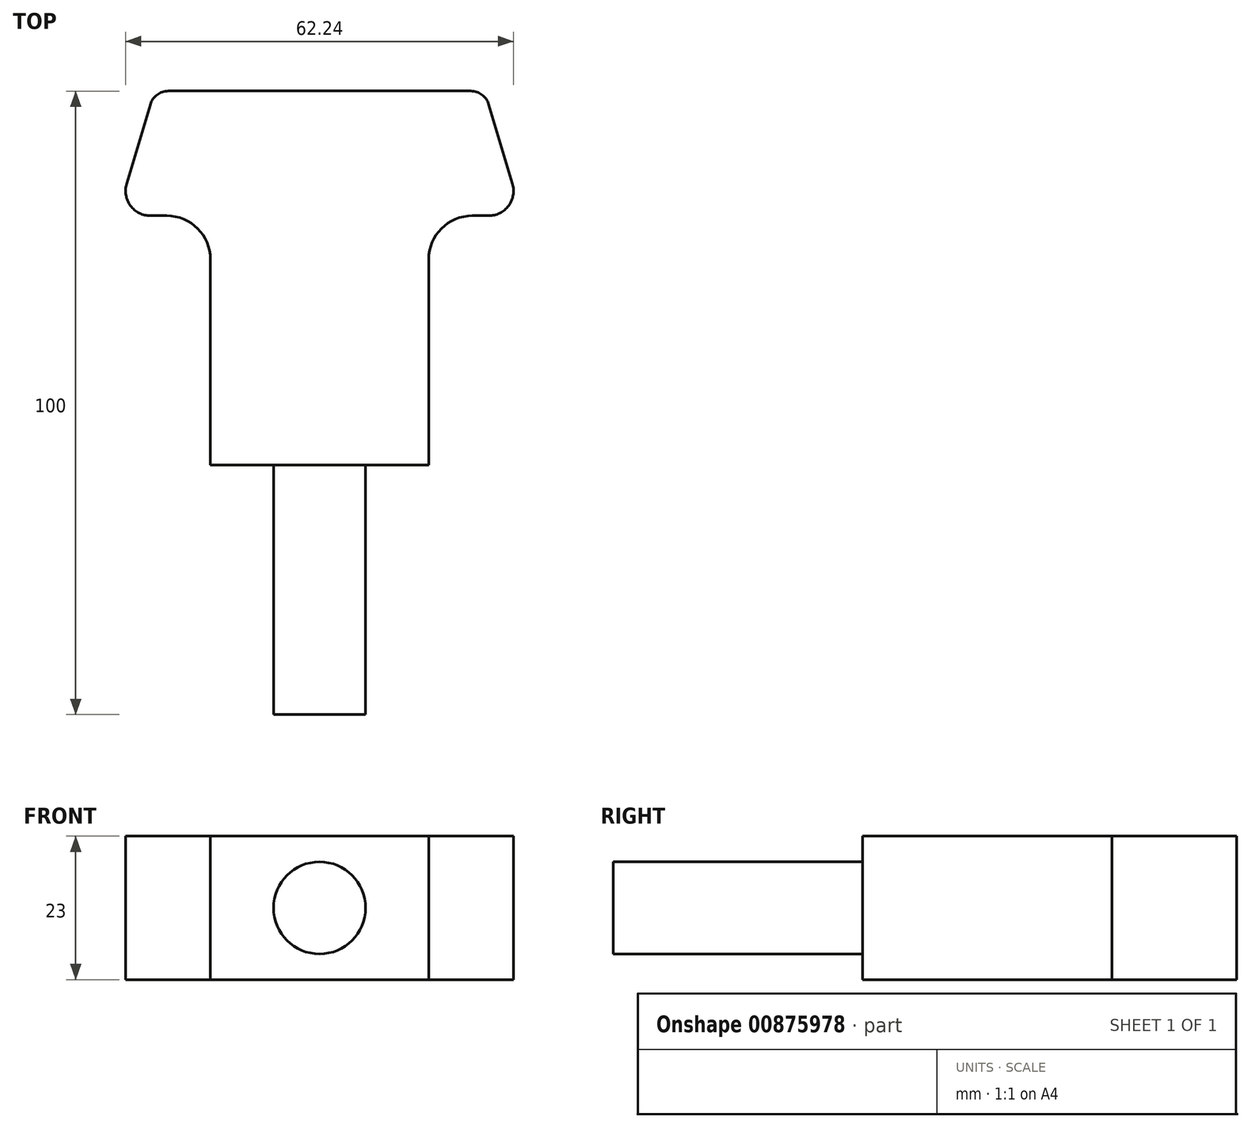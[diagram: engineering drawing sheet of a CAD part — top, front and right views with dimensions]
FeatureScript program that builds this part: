
annotation { "Feature Type Name" : "Feature", "Feature Type Description" : "" }
export const myFeature = defineFeature(function(context is Context, id is Id, definition is map)
    precondition{}
    {
        {
            var Q0;
            Q0=qCreatedBy(makeId("Top.planeOp"),FACE);
            var sketch = newSketch(context, id + "F0", { "sketchPlane" : qUnion([Q0])});
            skLineSegment(sketch, "E0", {"start": v(-33.37, 31.07) * mm, "end": v(19.63, 31.07) * mm});
            skLineSegment(sketch, "E1", {"start": v(-6.87, 31.07) * mm, "end": v(-6.87, 11.07) * mm, "construction": true});
            skLineSegment(sketch, "E2", {"start": v(-39.37, 11.07) * mm, "end": v(25.63, 11.07) * mm});
            skPoint(sketch, "E3", {"position": v(-6.87, 11.07) * mm});
            skLineSegment(sketch, "E4", {"start": v(-33.37, 31.07) * mm, "end": v(-39.37, 11.07) * mm});
            skLineSegment(sketch, "E5", {"start": v(19.63, 31.07) * mm, "end": v(25.63, 11.07) * mm});
            skLineSegment(sketch, "E6", {"start": v(-24.37, 11.07) * mm, "end": v(-24.37, -28.93) * mm});
            skLineSegment(sketch, "E7", {"start": v(10.63, 11.07) * mm, "end": v(10.63, -28.93) * mm});
            skLineSegment(sketch, "E8", {"start": v(-24.37, -28.93) * mm, "end": v(10.63, -28.93) * mm});
            skSolve(sketch);
        }
        {
            var Q0;
            {var subQ0=sQuery(id+"F0.wireOp",EDGE,"E6");Q0=makeQuery(id+"F0.imprint","IMPRINT",FACE,{"disambiguationData":[TD([[makeQuery(id+"F0.imprint","IMPRINT",EDGE,{"derivedFrom":subQ0}),1.0]])]});}
            var Q1;
            Q1=makeQuery(id+"F0.imprint","IMPRINT",FACE,{"disambiguationData":[TD([[makeQuery(id+"F0.imprint","IMPRINT",EDGE,{"derivedFrom":sQuery(id+"F0.wireOp",EDGE,"E0")}),-1.0]])]});
            extrude(context, id + "F1", {"entities" : qUnion([Q0, Q1]), "depth" : 23 * mm, "offsetDistance" : 25 * mm});
        }
        {
            var Q0;
            Q0=makeQuery(id+"F1.opExtrude","SWEPT_EDGE",EDGE,{"disambiguationData":[OSD([sQuery(id+"F0.wireOp",EDGE,"E0"),sQuery(id+"F0.wireOp",EDGE,"E4")])]});
            var Q1;
            Q1=makeQuery(id+"F1.opExtrude","SWEPT_EDGE",EDGE,{"disambiguationData":[OSD([sQuery(id+"F0.wireOp",EDGE,"E0"),sQuery(id+"F0.wireOp",EDGE,"E5")])]});
            fillet(context, id + "F2", {"entities" : qUnion([Q0, Q1]), "radius" : 3 * mm, "tangentPropagation" : true, "allowEdgeOverflow" : false});
        }
        {
            var Q0;
            Q0=makeQuery(id+"F1.opExtrude","SWEPT_EDGE",EDGE,{"disambiguationData":[OSD([sQuery(id+"F0.wireOp",EDGE,"E2"),sQuery(id+"F0.wireOp",EDGE,"E4")])]});
            var Q1;
            Q1=makeQuery(id+"F1.opExtrude","SWEPT_EDGE",EDGE,{"disambiguationData":[OSD([sQuery(id+"F0.wireOp",EDGE,"E2"),sQuery(id+"F0.wireOp",EDGE,"E5")])]});
            fillet(context, id + "F3", {"entities" : qUnion([Q0, Q1]), "radius" : 4 * mm, "tangentPropagation" : true, "allowEdgeOverflow" : false});
        }
        {
            var Q0;
            Q0=makeQuery(id+"F1.opExtrude","SWEPT_EDGE",EDGE,{"disambiguationData":[OSD([sQuery(id+"F0.wireOp",EDGE,"E2"),sQuery(id+"F0.wireOp",EDGE,"E6")])]});
            var Q1;
            Q1=makeQuery(id+"F1.opExtrude","SWEPT_EDGE",EDGE,{"disambiguationData":[OSD([sQuery(id+"F0.wireOp",EDGE,"E2"),sQuery(id+"F0.wireOp",EDGE,"E7")])]});
            fillet(context, id + "F4", {"entities" : qUnion([Q0, Q1]), "radius" : 7 * mm, "tangentPropagation" : true, "allowEdgeOverflow" : false});
        }
        {
            var Q0;
            Q0=makeQuery(id+"F1.opExtrude","SWEPT_FACE",FACE,{"disambiguationData":[OSD([sQuery(id+"F0.wireOp",EDGE,"E8")])]});
            var sketch = newSketch(context, id + "F5", { "sketchPlane" : qUnion([Q0])});
            skCircle(sketch, "E9", {"center": v(-6.87, 11.5) * mm, "radius": 7.38 * mm});
            skPoint(sketch, "E9.centerSnap0", {"position": v(-24.37, 11.5) * mm});
            skPoint(sketch, "E9.centerSnap1", {"position": v(-6.87, 23) * mm});
            skSolve(sketch);
        }
        {
            var Q0;
            Q0 = qSketchRegion(id + "F5", true);
            extrude(context, id + "F6", {"entities" : qUnion([Q0]), "operationType" : NewBodyOperationType.ADD, "depth" : 40 * mm, "offsetDistance" : 25 * mm});
        }
    });
